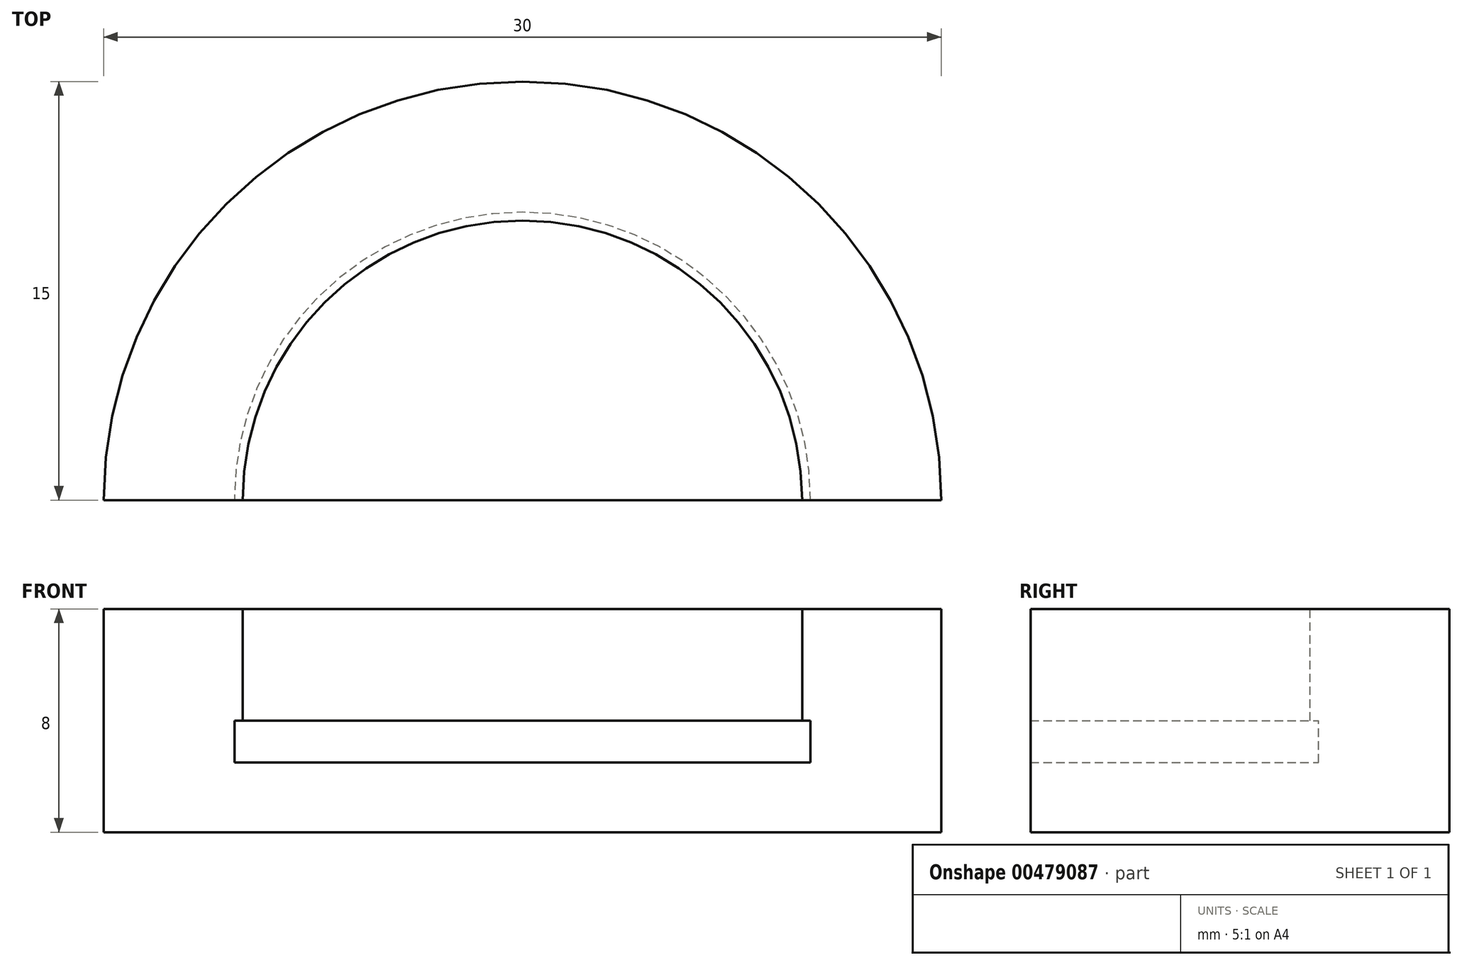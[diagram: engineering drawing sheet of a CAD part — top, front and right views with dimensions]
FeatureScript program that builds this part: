
annotation { "Feature Type Name" : "Feature", "Feature Type Description" : "" }
export const myFeature = defineFeature(function(context is Context, id is Id, definition is map)
    precondition{}
    {
        {
            var Q0;
            Q0=qCreatedBy(makeId("Front.planeOp"),FACE);
            var sketch = newSketch(context, id + "F0", { "sketchPlane" : qUnion([Q0])});
            skLineSegment(sketch, "E0", {"start": v(8.83, -2.12) * mm, "end": v(-6.17, -2.12) * mm});
            skLineSegment(sketch, "E1", {"start": v(-6.17, -2.12) * mm, "end": v(-6.17, 5.88) * mm});
            skLineSegment(sketch, "E2", {"start": v(-6.17, 5.88) * mm, "end": v(-1.18, 5.88) * mm});
            skLineSegment(sketch, "E3", {"start": v(-1.18, 5.88) * mm, "end": v(-1.18, 1.88) * mm});
            skLineSegment(sketch, "E4", {"start": v(-1.18, 1.88) * mm, "end": v(-1.48, 1.88) * mm});
            skLineSegment(sketch, "E5", {"start": v(-1.48, 1.88) * mm, "end": v(-1.48, 0.38) * mm});
            skLineSegment(sketch, "E6", {"start": v(-1.48, 0.38) * mm, "end": v(8.83, 0.38) * mm});
            skLineSegment(sketch, "E7", {"start": v(8.83, 0.38) * mm, "end": v(8.83, -2.12) * mm});
            skSolve(sketch);
        }
        {
            var Q0;
            Q0=makeQuery(id+"F0.imprint","IMPRINT",FACE,{"disambiguationData":[TD([[makeQuery(id+"F0.imprint","IMPRINT",EDGE,{"derivedFrom":sQuery(id+"F0.wireOp",EDGE,"E0")}),-1.0]])]});
            var Q1;
            Q1=sQuery(id+"F0.wireOp",EDGE,"E7");
            revolve(context, id + "F1", {"entities" : qUnion([Q0]), "axis" : qUnion([Q1]), "revolveType" : RevolveType.ONE_DIRECTION, "angle" : 180 * degree});
        }
    });
